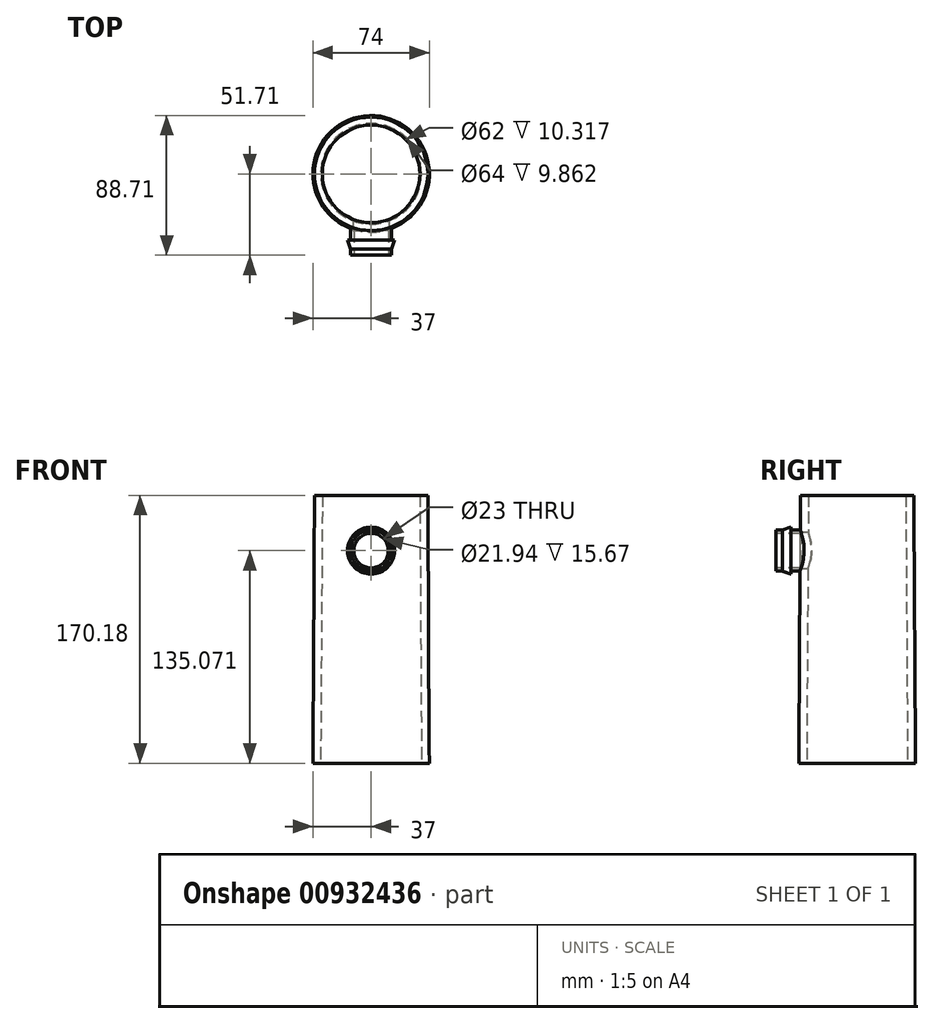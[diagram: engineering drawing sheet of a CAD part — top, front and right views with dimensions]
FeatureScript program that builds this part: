
annotation { "Feature Type Name" : "Feature", "Feature Type Description" : "" }
export const myFeature = defineFeature(function(context is Context, id is Id, definition is map)
    precondition{}
    {
        {
            var Q0;
            Q0=qCreatedBy(makeId("Front.planeOp"),FACE);
            var sketch = newSketch(context, id + "F0", { "sketchPlane" : qUnion([Q0])});
            skLineSegment(sketch, "E0", {"start": v(0, -152.93) * mm, "end": v(0, -2.93) * mm});
            skLineSegment(sketch, "E1", {"start": v(0, -152.93) * mm, "end": v(-32, -152.93) * mm});
            skLineSegment(sketch, "E2", {"start": v(0, -2.93) * mm, "end": v(-31, -2.93) * mm});
            skLineSegment(sketch, "E3", {"start": v(-31, -2.93) * mm, "end": v(-32, -152.93) * mm});
            skLineSegment(sketch, "E4", {"start": v(-31, -2.93) * mm, "end": v(-31, 7.39) * mm});
            skLineSegment(sketch, "E5", {"start": v(-32, -152.93) * mm, "end": v(-32, -162.8) * mm});
            skLineSegment(sketch, "E6", {"start": v(-31, 7.39) * mm, "end": v(-36, 7.39) * mm});
            skLineSegment(sketch, "E7", {"start": v(-32, -162.8) * mm, "end": v(-37, -162.8) * mm});
            skLineSegment(sketch, "E8", {"start": v(-36, 7.39) * mm, "end": v(-36, -3.52) * mm});
            skLineSegment(sketch, "E9", {"start": v(-36, -3.52) * mm, "end": v(-36.9, -152.61) * mm});
            skLineSegment(sketch, "E10", {"start": v(-36.9, -152.61) * mm, "end": v(-37, -162.8) * mm});
            skSolve(sketch);
        }
        {
            var Q0;
            Q0=makeQuery(id+"F0.imprint","IMPRINT",FACE,{"disambiguationData":[TD([[makeQuery(id+"F0.imprint","IMPRINT",EDGE,{"derivedFrom":sQuery(id+"F0.wireOp",EDGE,"E3")}),-1.0]])]});
            var Q1;
            Q1=sQuery(id+"F0.wireOp",EDGE,"E0");
            revolve(context, id + "F1", {"surfaceOperationType" : NewSurfaceOperationType.NEW, "entities" : qUnion([Q0]), "axis" : qUnion([Q1]), "revolveType" : RevolveType.FULL});
        }
        {
            var Q0;
            Q0=qCreatedBy(makeId("Front.planeOp"),FACE);
            cPlane(context, id + "F2", {"entities" : qUnion([Q0]), "cplaneType" : CPlaneType.OFFSET, "offset" : 45 * mm, "width" : 150 * mm, "height" : 150 * mm});
        }
        {
            var Q0;
            Q0=qCreatedBy(id+"F2.planeOp",FACE);
            var sketch = newSketch(context, id + "F3", { "sketchPlane" : qUnion([Q0])});
            skCircle(sketch, "E11", {"center": v(0, -27.72) * mm, "radius": 11.5 * mm});
            skCircle(sketch, "E12", {"center": v(0, -27.72) * mm, "radius": 13 * mm});
            skSolve(sketch);
        }
        {
            var Q0;
            Q0=makeQuery(id+"F3.imprint","IMPRINT",FACE,{"disambiguationData":[TD([[makeQuery(id+"F3.imprint","IMPRINT",EDGE,{"derivedFrom":sQuery(id+"F3.wireOp",EDGE,"E11")}),-1.0]])]});
            extrude(context, id + "F4", {"entities" : qUnion([Q0]), "operationType" : NewBodyOperationType.ADD, "endBound" : BoundingType.UP_TO_NEXT, "oppositeDirection" : true, "depth" : 25 * mm, "offsetDistance" : 25 * mm});
        }
        {
            var Q0;
            Q0=makeQuery(id+"F3.imprint","IMPRINT",FACE,{"disambiguationData":[TD([[makeQuery(id+"F3.imprint","IMPRINT",EDGE,{"derivedFrom":sQuery(id+"F3.wireOp",EDGE,"E11")}),1.0]])]});
            extrude(context, id + "F5", {"entities" : qUnion([Q0]), "operationType" : NewBodyOperationType.REMOVE, "oppositeDirection" : true, "depth" : 25 * mm, "offsetDistance" : 25 * mm});
        }
        {
            var Q0;
            Q0=qCreatedBy(makeId("Right.planeOp"),FACE);
            var sketch = newSketch(context, id + "F6", { "sketchPlane" : qUnion([Q0])});
            skLineSegment(sketch, "E13", {"start": v(-45.05, -27.72) * mm, "end": v(-29.8, -27.72) * mm});
            skLineSegment(sketch, "E14", {"start": v(-36.08, -14.72) * mm, "end": v(-42.1, -14.72) * mm});
            skLineSegment(sketch, "E15", {"start": v(-42.1, -14.72) * mm, "end": v(-47.6, -14.72) * mm});
            skLineSegment(sketch, "E16", {"start": v(-47.6, -14.72) * mm, "end": v(-51.71, -14.72) * mm});
            skLineSegment(sketch, "E17", {"start": v(-51.71, -14.72) * mm, "end": v(-51.71, -16.75) * mm});
            skLineSegment(sketch, "E18", {"start": v(-51.71, -16.75) * mm, "end": v(-36.04, -16.75) * mm});
            skLineSegment(sketch, "E19", {"start": v(-36.04, -16.75) * mm, "end": v(-36.08, -14.72) * mm});
            skLineSegment(sketch, "E20", {"start": v(-42.1, -14.72) * mm, "end": v(-42.1, -12.78) * mm});
            skLineSegment(sketch, "E21", {"start": v(-42.1, -12.78) * mm, "end": v(-47.6, -14.72) * mm});
            skSolve(sketch);
        }
        {
            var Q0;
            Q0=makeQuery(id+"F6.imprint","IMPRINT",FACE,{"disambiguationData":[TD([[makeQuery(id+"F6.imprint","IMPRINT",EDGE,{"derivedFrom":sQuery(id+"F6.wireOp",EDGE,"E14")}),1.0]])]});
            var Q1;
            Q1=makeQuery(id+"F6.imprint","IMPRINT",FACE,{"disambiguationData":[TD([[makeQuery(id+"F6.imprint","IMPRINT",EDGE,{"derivedFrom":sQuery(id+"F6.wireOp",EDGE,"E15")}),-1.0]])]});
            var Q2;
            Q2=sQuery(id+"F6.wireOp",EDGE,"E13");
            revolve(context, id + "F7", {"operationType" : NewBodyOperationType.ADD, "surfaceOperationType" : NewSurfaceOperationType.NEW, "entities" : qUnion([Q0, Q1]), "axis" : qUnion([Q2]), "revolveType" : RevolveType.FULL});
        }
    });
